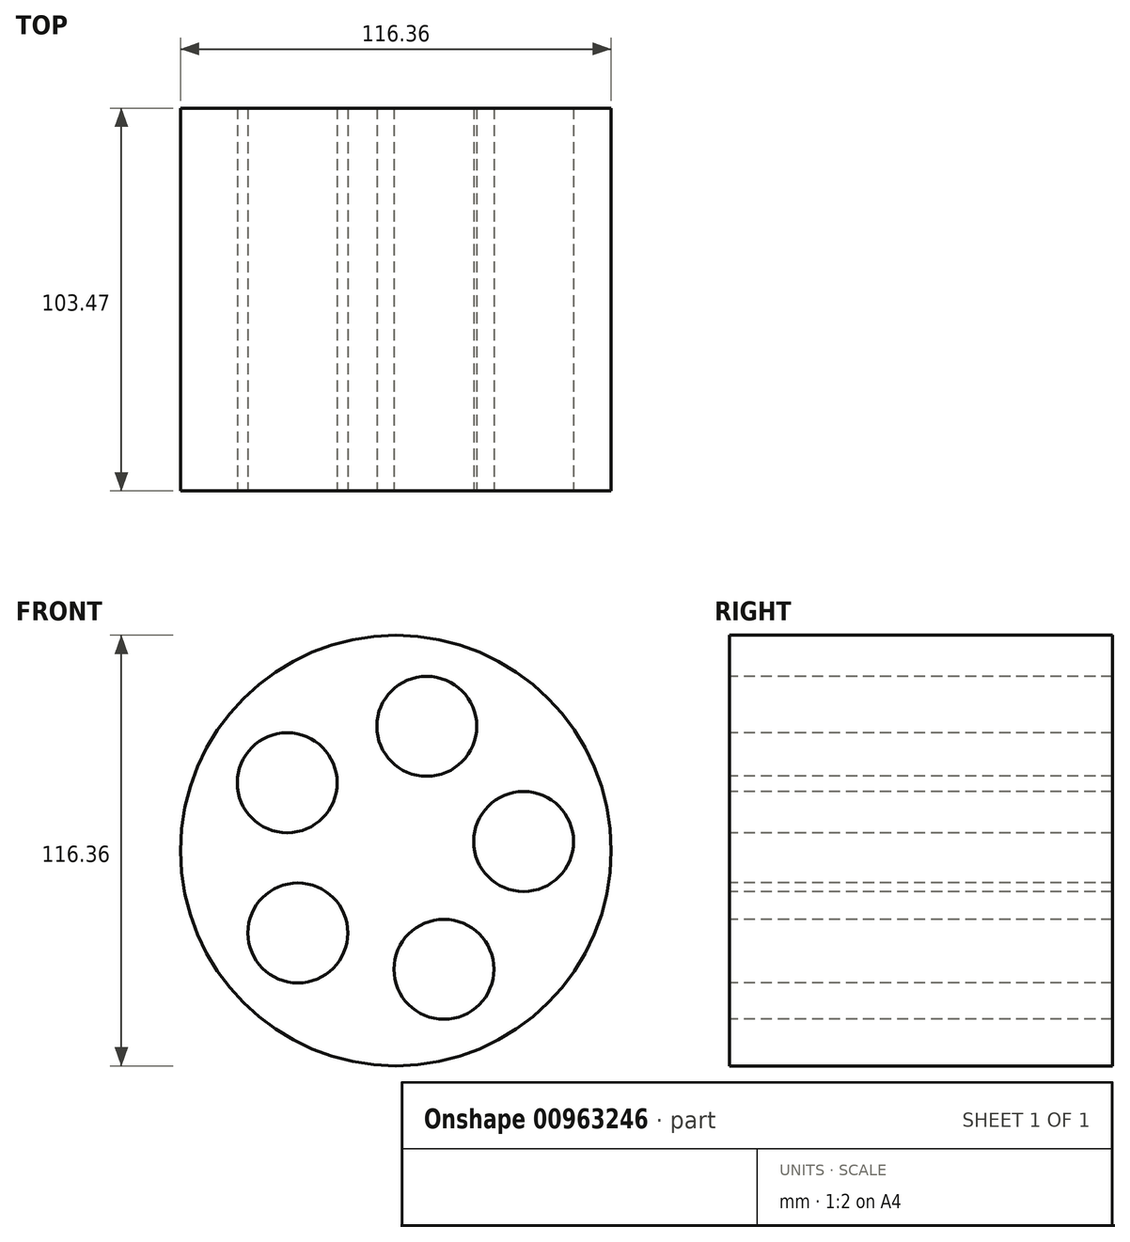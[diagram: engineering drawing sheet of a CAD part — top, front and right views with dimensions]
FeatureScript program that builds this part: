
annotation { "Feature Type Name" : "Feature", "Feature Type Description" : "" }
export const myFeature = defineFeature(function(context is Context, id is Id, definition is map)
    precondition{}
    {
        {
            var Q0;
            Q0=qCreatedBy(makeId("Front.planeOp"),FACE);
            var sketch = newSketch(context, id + "F0", { "sketchPlane" : qUnion([Q0])});
            skCircle(sketch, "E0", {"center": v(0, 0) * mm, "radius": 58.18 * mm});
            skSolve(sketch);
        }
        {
            var Q0;
            Q0=makeQuery(id+"F0.imprint","IMPRINT",FACE,{"disambiguationData":[TD([[makeQuery(id+"F0.imprint","IMPRINT",EDGE,{"derivedFrom":sQuery(id+"F0.wireOp",EDGE,"E0")}),1.0]])]});
            extrude(context, id + "F1", {"entities" : qUnion([Q0]), "depth" : 103.47 * mm, "offsetDistance" : 25.4 * mm});
        }
        {
            var Q0;
            Q0=makeQuery(id+"F1.opExtrude","CAP_FACE",FACE,{"disambiguationData":[OSD([sQuery(id+"F0.wireOp",EDGE,"E0")])],"isStart":false});
            var sketch = newSketch(context, id + "F2", { "sketchPlane" : qUnion([Q0])});
            skCircle(sketch, "E1", {"center": v(8.35, 33.58) * mm, "radius": 13.5 * mm});
            skCircle(sketch, "E2.1.0", {"center": v(34.52, 2.44) * mm, "radius": 13.5 * mm});
            skCircle(sketch, "E2.2.0", {"center": v(12.99, -32.08) * mm, "radius": 13.5 * mm});
            skCircle(sketch, "E2.3.0", {"center": v(-26.5, -22.26) * mm, "radius": 13.5 * mm});
            skCircle(sketch, "E2.4.0", {"center": v(-29.36, 18.32) * mm, "radius": 13.5 * mm});
            skPoint(sketch, "E2.center", {"position": v(0, 0) * mm});
            skLineSegment(sketch, "E2.anchor1", {"start": v(0, 0) * mm, "end": v(8.35, 33.58) * mm, "construction": true});
            skLineSegment(sketch, "E2.anchor2", {"start": v(0, 0) * mm, "end": v(-29.36, 18.32) * mm, "construction": true});
            skSolve(sketch);
        }
        {
            var Q0;
            Q0=makeQuery(id+"F2.imprint","IMPRINT",FACE,{"disambiguationData":[TD([[makeQuery(id+"F2.imprint","IMPRINT",EDGE,{"derivedFrom":sQuery(id+"F2.wireOp",EDGE,"E1")}),1.0]])]});
            extrude(context, id + "F3", {"entities" : qUnion([Q0]), "operationType" : NewBodyOperationType.REMOVE, "oppositeDirection" : true, "depth" : 177.74 * mm, "offsetDistance" : 25.4 * mm});
        }
        {
            var Q0;
            Q0=makeQuery(id+"F2.imprint","IMPRINT",FACE,{"disambiguationData":[TD([[makeQuery(id+"F2.imprint","IMPRINT",EDGE,{"derivedFrom":sQuery(id+"F2.wireOp",EDGE,"E2.4.0")}),1.0]])]});
            var Q1;
            Q1=makeQuery(id+"F2.imprint","IMPRINT",FACE,{"disambiguationData":[TD([[makeQuery(id+"F2.imprint","IMPRINT",EDGE,{"derivedFrom":sQuery(id+"F2.wireOp",EDGE,"E2.3.0")}),1.0]])]});
            var Q2;
            Q2=makeQuery(id+"F2.imprint","IMPRINT",FACE,{"disambiguationData":[TD([[makeQuery(id+"F2.imprint","IMPRINT",EDGE,{"derivedFrom":sQuery(id+"F2.wireOp",EDGE,"E2.2.0")}),1.0]])]});
            var Q3;
            Q3=makeQuery(id+"F2.imprint","IMPRINT",FACE,{"disambiguationData":[TD([[makeQuery(id+"F2.imprint","IMPRINT",EDGE,{"derivedFrom":sQuery(id+"F2.wireOp",EDGE,"E2.1.0")}),1.0]])]});
            extrude(context, id + "F4", {"entities" : qUnion([Q0, Q1, Q2, Q3]), "operationType" : NewBodyOperationType.REMOVE, "oppositeDirection" : true, "depth" : 213.26 * mm, "offsetDistance" : 25.4 * mm});
        }
    });
